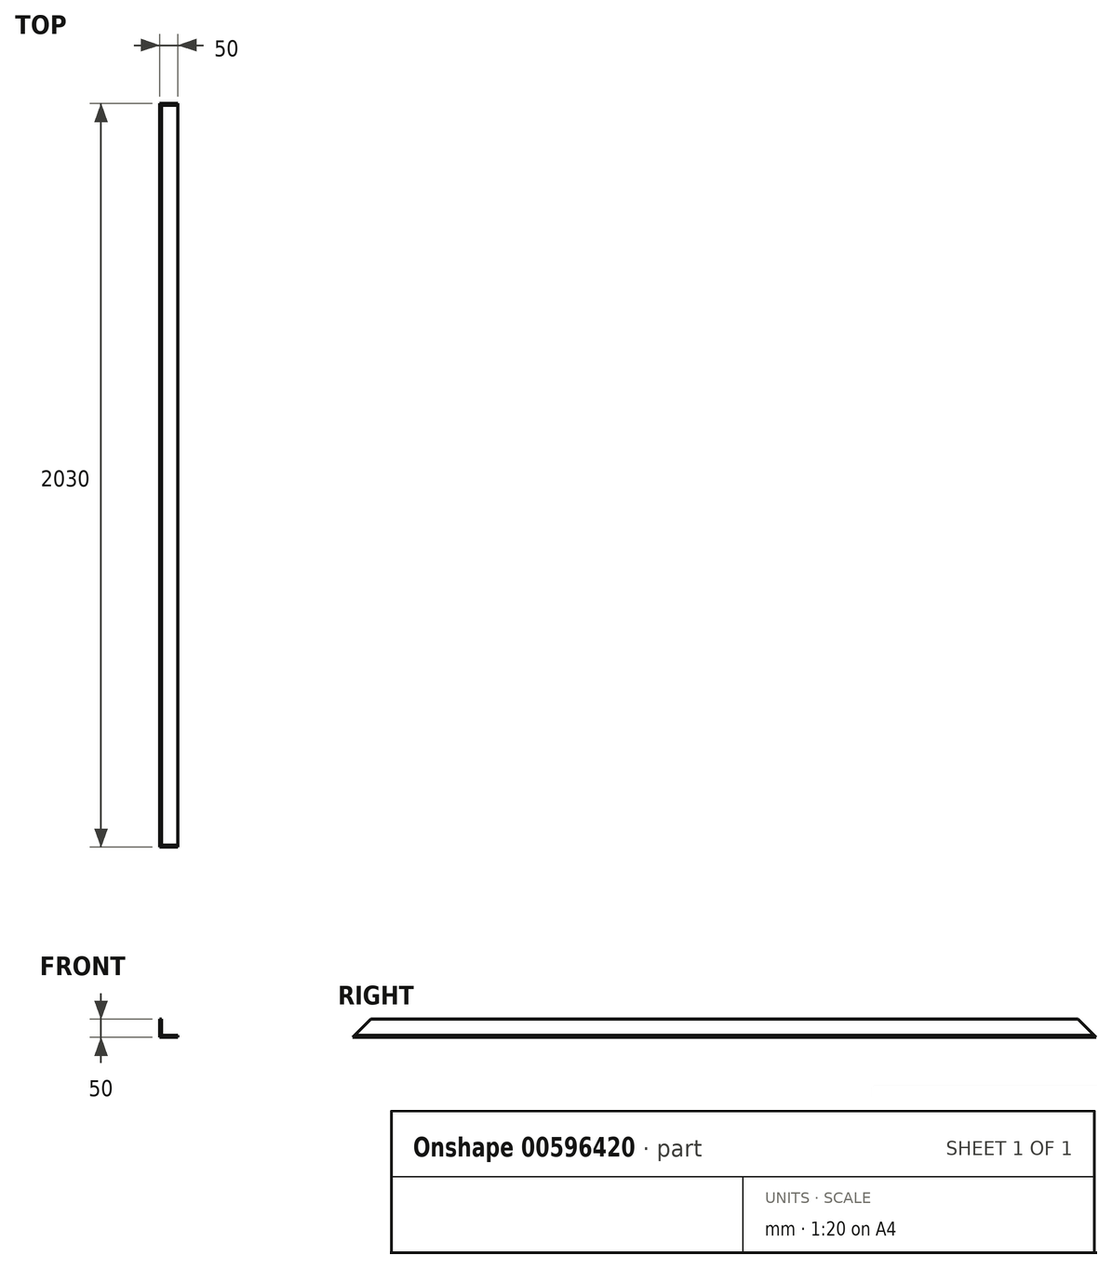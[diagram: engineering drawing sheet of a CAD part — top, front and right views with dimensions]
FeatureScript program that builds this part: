
annotation { "Feature Type Name" : "Feature", "Feature Type Description" : "" }
export const myFeature = defineFeature(function(context is Context, id is Id, definition is map)
    precondition{}
    {
        {
            var Q0;
            Q0=qCreatedBy(makeId("Front.planeOp"),FACE);
            var sketch = newSketch(context, id + "F0", { "sketchPlane" : qUnion([Q0])});
            skLineSegment(sketch, "E0", {"start": v(0, 0) * mm, "end": v(50, 0) * mm});
            skLineSegment(sketch, "E1", {"start": v(0, 0) * mm, "end": v(0, 50) * mm});
            skLineSegment(sketch, "E2.0", {"start": v(5, 5) * mm, "end": v(5, 50) * mm});
            skLineSegment(sketch, "E2.1", {"start": v(5, 5) * mm, "end": v(50, 5) * mm});
            skLineSegment(sketch, "E3", {"start": v(5, 50) * mm, "end": v(0, 50) * mm});
            skLineSegment(sketch, "E4", {"start": v(50, 5) * mm, "end": v(50, 0) * mm});
            skSolve(sketch);
        }
        {
            var Q0;
            Q0=makeQuery(id+"F0.imprint","IMPRINT",FACE,{"disambiguationData":[TD([[makeQuery(id+"F0.imprint","IMPRINT",EDGE,{"derivedFrom":sQuery(id+"F0.wireOp",EDGE,"E0")}),1.0]])]});
            extrude(context, id + "F1", {"entities" : qUnion([Q0]), "endBound" : BoundingType.SYMMETRIC, "depth" : 2030 * mm, "offsetDistance" : 25 * mm});
        }
        {
            var Q0;
            Q0=makeQuery(id+"F1.opExtrude","SWEPT_FACE",FACE,{"disambiguationData":[OSD([sQuery(id+"F0.wireOp",EDGE,"E1")])]});
            var sketch = newSketch(context, id + "F2", { "sketchPlane" : qUnion([Q0])});
            skLineSegment(sketch, "E5", {"start": v(1015, 0) * mm, "end": v(965, 50) * mm});
            skLineSegment(sketch, "E6", {"start": v(-1015, 0) * mm, "end": v(-965, 50) * mm});
            skSolve(sketch);
        }
        {
            var Q0;
            {var subQ0=sQuery(id+"F2.wireOp",EDGE,"E6");Q0=makeQuery(id+"F2.imprint","IMPRINT",FACE,{"disambiguationData":[TD([[makeQuery(id+"F2.imprint","IMPRINT",EDGE,{"derivedFrom":subQ0}),1.0]])]});}
            var Q1;
            {var subQ0=sQuery(id+"F2.wireOp",EDGE,"E5");Q1=makeQuery(id+"F2.imprint","IMPRINT",FACE,{"disambiguationData":[TD([[makeQuery(id+"F2.imprint","IMPRINT",EDGE,{"derivedFrom":subQ0}),-1.0]])]});}
            extrude(context, id + "F3", {"entities" : qUnion([Q0, Q1]), "operationType" : NewBodyOperationType.REMOVE, "oppositeDirection" : true, "depth" : 50 * mm, "offsetDistance" : 25 * mm});
        }
    });
